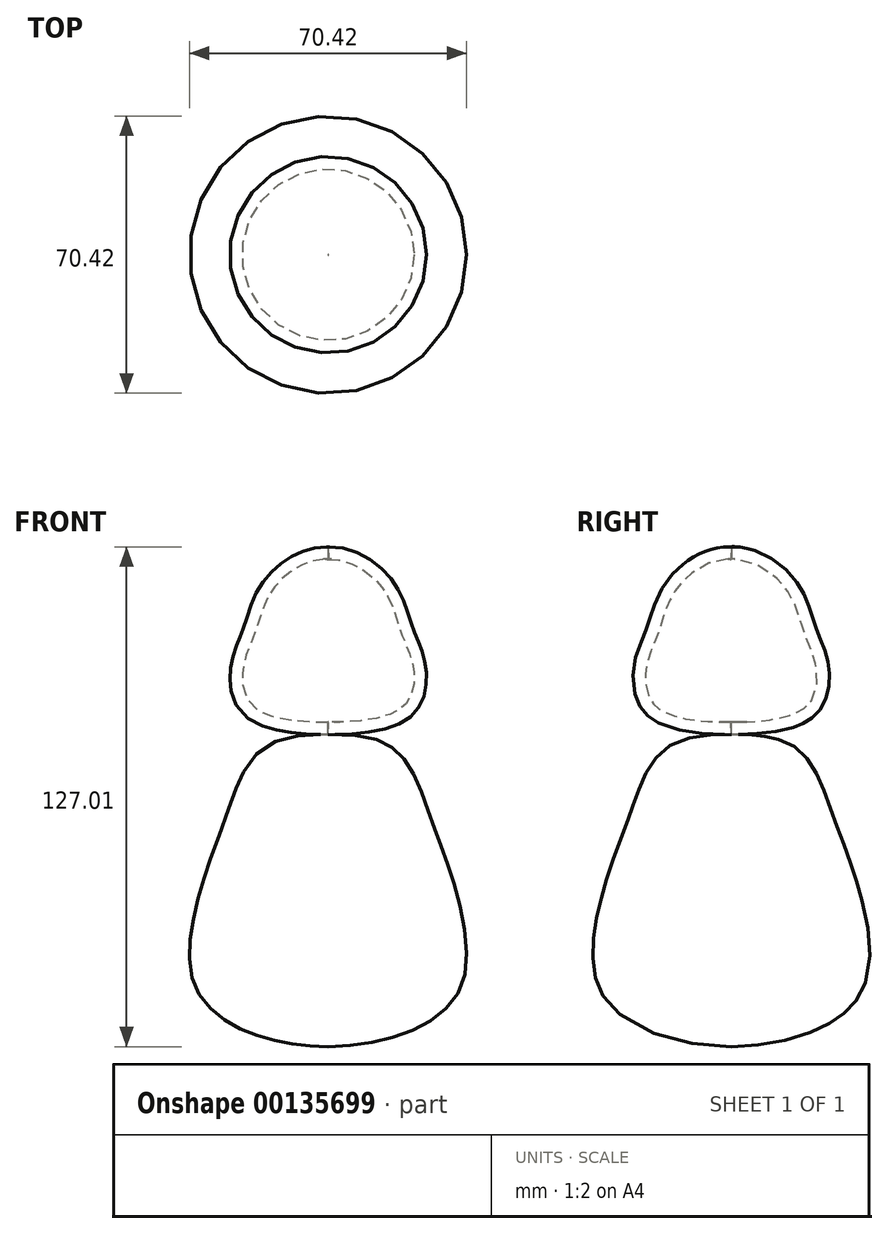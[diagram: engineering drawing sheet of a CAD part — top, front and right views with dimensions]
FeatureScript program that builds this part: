
annotation { "Feature Type Name" : "Feature", "Feature Type Description" : "" }
export const myFeature = defineFeature(function(context is Context, id is Id, definition is map)
    precondition{}
    {
        {
            var Q0;
            Q0=qCreatedBy(makeId("Front.planeOp"),FACE);
            var sketch = newSketch(context, id + "F0", { "sketchPlane" : qUnion([Q0])});
            skFitSpline(sketch, "E0", {"points": [v(0, 47.63) * mm, v(16.37, 38.98) * mm, v(21.56, 26.9) * mm, v(24.72, 17.54) * mm, v(21.59, 5.04) * mm, v(0, 0) * mm], "startDerivative": vector(89.65, 2.34) * mm, "endDerivative": vector(-99.52, 2.12) * mm});
            skLineSegment(sketch, "E1", {"start": v(0, 0) * mm, "end": v(0, 47.63) * mm});
            skFitSpline(sketch, "E2.0", {"points": [v(0.08, 44.45) * mm, v(0.83, 44.47) * mm, v(2.31, 44.38) * mm, v(4.53, 43.86) * mm, v(6.69, 43.02) * mm, v(8.74, 41.88) * mm, v(10.64, 40.5) * mm, v(12.04, 39.2) * mm, v(13.02, 38.12) * mm, v(13.7, 37.29) * mm, v(14.29, 36.45) * mm, v(15, 35.3) * mm, v(15.76, 33.8) * mm, v(16.53, 31.93) * mm, v(17.09, 30.32) * mm, v(17.51, 29) * mm, v(17.83, 28.02) * mm, v(18.15, 27.02) * mm, v(18.44, 26.18) * mm, v(18.68, 25.52) * mm, v(18.92, 24.87) * mm, v(19.23, 24.09) * mm, v(19.59, 23.2) * mm, v(20.06, 22.06) * mm, v(20.6, 20.7) * mm, v(21.04, 19.4) * mm, v(21.33, 18.34) * mm, v(21.5, 17.52) * mm, v(21.65, 16.68) * mm, v(21.78, 15.49) * mm, v(21.83, 13.93) * mm, v(21.66, 12.07) * mm, v(21.23, 10.33) * mm, v(20.67, 9.05) * mm, v(20.1, 8.15) * mm, v(19.61, 7.54) * mm, v(19.05, 7) * mm, v(18.36, 6.46) * mm, v(17.55, 5.95) * mm, v(16.31, 5.32) * mm, v(14.48, 4.64) * mm, v(11.93, 4) * mm, v(9.12, 3.54) * mm, v(5.15, 3.17) * mm, v(2.06, 3.13) * mm, v(0.07, 3.17) * mm]});
            skLineSegment(sketch, "E3", {"start": v(0, 47.63) * mm, "end": v(0.08, 44.45) * mm});
            skLineSegment(sketch, "E4", {"start": v(0.07, 3.17) * mm, "end": v(0, 0) * mm});
            skSolve(sketch);
        }
        {
            var Q0;
            Q0=makeQuery(id+"F0.imprint","IMPRINT",FACE,{"disambiguationData":[TD([[makeQuery(id+"F0.imprint","IMPRINT",EDGE,{"derivedFrom":sQuery(id+"F0.wireOp",EDGE,"E1")}),-1.0]])]});
            var Q1;
            Q1=makeQuery(id+"F0.imprint","IMPRINT",FACE,{"disambiguationData":[TD([[makeQuery(id+"F0.imprint","IMPRINT",EDGE,{"derivedFrom":sQuery(id+"F0.wireOp",EDGE,"E0")}),-1.0]])]});
            var Q2;
            Q2=sQuery(id+"F0.wireOp",EDGE,"E1");
            revolve(context, id + "F1", {"entities" : qUnion([Q0, Q1]), "axis" : qUnion([Q2]), "revolveType" : RevolveType.FULL});
        }
        {
            var Q0;
            Q0=makeQuery(id+"F0.imprint","IMPRINT",FACE,{"disambiguationData":[TD([[makeQuery(id+"F0.imprint","IMPRINT",EDGE,{"derivedFrom":sQuery(id+"F0.wireOp",EDGE,"E1")}),-1.0]])]});
            var Q1;
            Q1=sQuery(id+"F0.wireOp",EDGE,"E1");
            revolve(context, id + "F2", {"entities" : qUnion([Q0]), "axis" : qUnion([Q1]), "revolveType" : RevolveType.FULL, "oppositeDirection" : true});
        }
        {
            var Q0;
            Q0=qCreatedBy(makeId("Front.planeOp"),FACE);
            var sketch = newSketch(context, id + "F3", { "sketchPlane" : qUnion([Q0])});
            skFitSpline(sketch, "E5", {"points": [v(0, 0) * mm, v(18.83, -5.6) * mm, v(26.02, -21.15) * mm, v(32.06, -38.2) * mm, v(34.28, -62.71) * mm, v(21.56, -75.16) * mm, v(0, -79.37) * mm], "startDerivative": vector(180.7, 0) * mm, "endDerivative": vector(-129.3, -1.37) * mm});
            skLineSegment(sketch, "E6", {"start": v(0, 0) * mm, "end": v(0, -79.37) * mm});
            skSolve(sketch);
        }
        {
            var Q0;
            Q0=makeQuery(id+"F3.imprint","IMPRINT",FACE,{"disambiguationData":[TD([[makeQuery(id+"F3.imprint","IMPRINT",EDGE,{"derivedFrom":sQuery(id+"F3.wireOp",EDGE,"E5")}),-1.0]])]});
            var Q1;
            Q1=sQuery(id+"F3.wireOp",EDGE,"E6");
            revolve(context, id + "F4", {"entities" : qUnion([Q0]), "axis" : qUnion([Q1]), "revolveType" : RevolveType.FULL});
        }
    });
